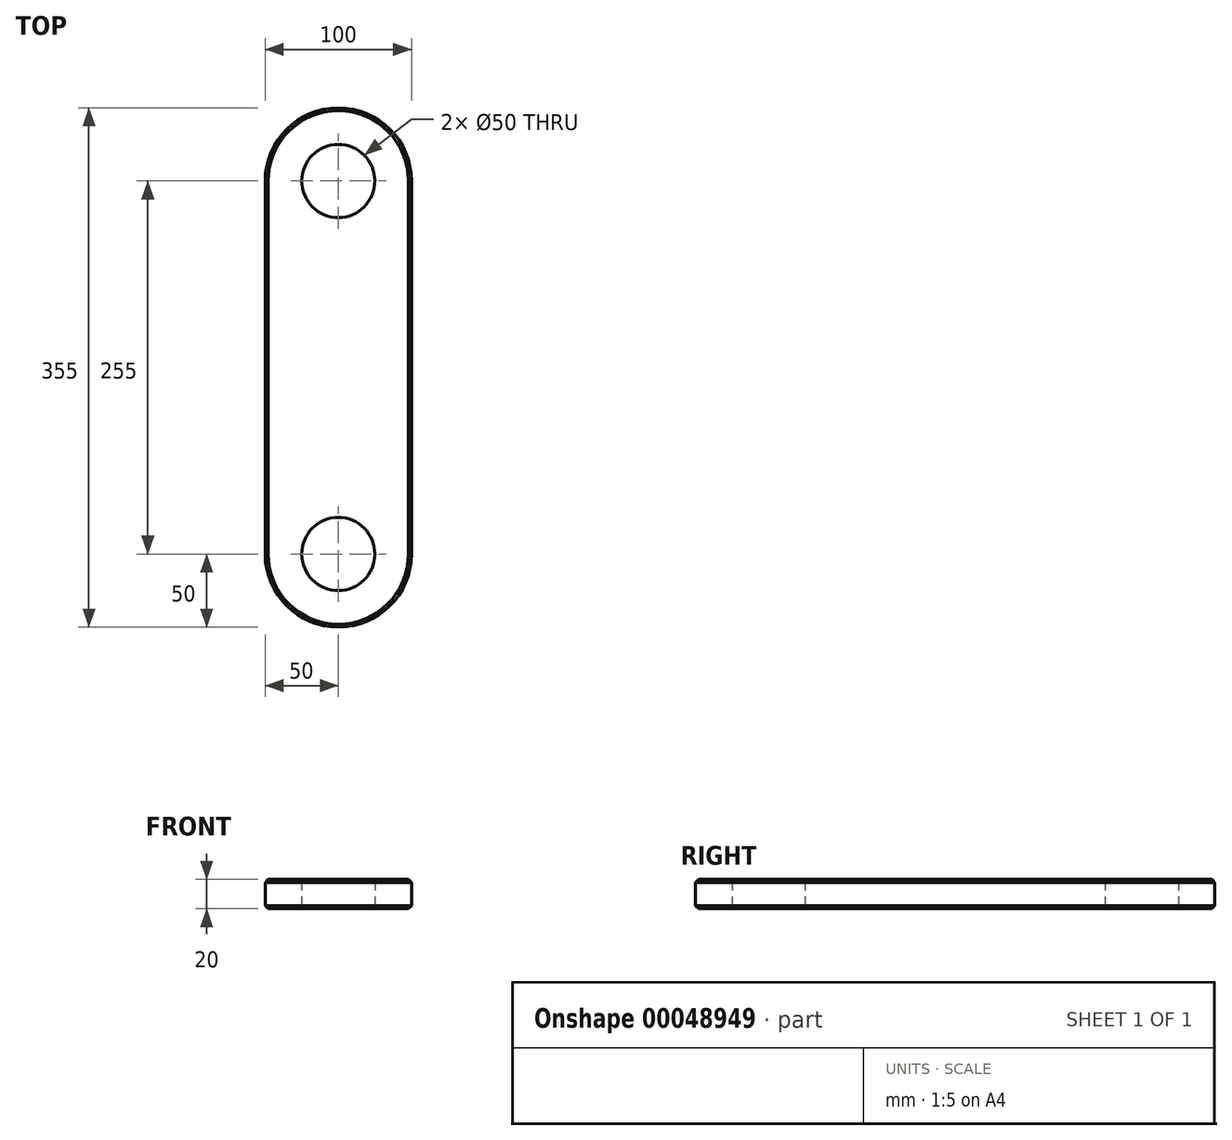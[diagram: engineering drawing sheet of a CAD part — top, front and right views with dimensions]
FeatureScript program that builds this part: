
annotation { "Feature Type Name" : "Feature", "Feature Type Description" : "" }
export const myFeature = defineFeature(function(context is Context, id is Id, definition is map)
    precondition{}
    {
        {
            var Q0;
            Q0=qCreatedBy(makeId("Top.planeOp"),FACE);
            var sketch = newSketch(context, id + "F0", { "sketchPlane" : qUnion([Q0])});
            skLineSegment(sketch, "E0.rect.bottom", {"start": v(50, 127.5) * mm, "end": v(-50, 127.5) * mm});
            skLineSegment(sketch, "E0.rect.top", {"start": v(50, -127.5) * mm, "end": v(-50, -127.5) * mm});
            skLineSegment(sketch, "E0.rect.left", {"start": v(50, 127.5) * mm, "end": v(50, -127.5) * mm});
            skLineSegment(sketch, "E0.rect.right", {"start": v(-50, 127.5) * mm, "end": v(-50, -127.5) * mm});
            skPoint(sketch, "E0.rect.middle", {"position": v(0, 0) * mm});
            skCircle(sketch, "E1", {"center": v(0, 127.5) * mm, "radius": 50 * mm});
            skCircle(sketch, "E2", {"center": v(0, -127.5) * mm, "radius": 50 * mm});
            skCircle(sketch, "E3", {"center": v(0, 127.5) * mm, "radius": 25 * mm});
            skCircle(sketch, "E4", {"center": v(0, -127.5) * mm, "radius": 25 * mm});
            skSolve(sketch);
        }
        {
            var Q0;
            {var subQ0=sQuery(id+"F0.wireOp",EDGE,"E3");var subQ1=sQuery(id+"F0.wireOp",EDGE,"E0.rect.bottom");var subQ3=makeQuery(id+"F0.imprint","INTERSECT",VERTEX,{"disambiguationData":[OD(0.0)],"derivedFrom":[subQ1,subQ0]});Q0=makeQuery(id+"F0.imprint","IMPRINT",FACE,{"disambiguationData":[TD([[makeQuery(id+"F0.imprint","IMPRINT",EDGE,{"disambiguationData":[TD([[subQ3,-1.0]])],"derivedFrom":subQ0}),-1.0]])]});}
            var Q1;
            {var subQ3=sQuery(id+"F0.wireOp",EDGE,"E0.rect.left");Q1=makeQuery(id+"F0.imprint","IMPRINT",FACE,{"disambiguationData":[TD([[makeQuery(id+"F0.imprint","IMPRINT",EDGE,{"derivedFrom":subQ3}),-1.0]])]});}
            var Q2;
            {var subQ0=sQuery(id+"F0.wireOp",EDGE,"E3");var subQ1=sQuery(id+"F0.wireOp",EDGE,"E0.rect.bottom");var subQ3=makeQuery(id+"F0.imprint","INTERSECT",VERTEX,{"disambiguationData":[OD(0.0)],"derivedFrom":[subQ1,subQ0]});Q2=makeQuery(id+"F0.imprint","IMPRINT",FACE,{"disambiguationData":[TD([[makeQuery(id+"F0.imprint","IMPRINT",EDGE,{"disambiguationData":[TD([[subQ3,1.0]])],"derivedFrom":subQ0}),-1.0]])]});}
            var Q3;
            {var subQ0=sQuery(id+"F0.wireOp",EDGE,"E4");var subQ1=sQuery(id+"F0.wireOp",EDGE,"E0.rect.top");var subQ3=makeQuery(id+"F0.imprint","INTERSECT",VERTEX,{"disambiguationData":[OD(0.0)],"derivedFrom":[subQ1,subQ0]});Q3=makeQuery(id+"F0.imprint","IMPRINT",FACE,{"disambiguationData":[TD([[makeQuery(id+"F0.imprint","IMPRINT",EDGE,{"disambiguationData":[TD([[subQ3,-1.0]])],"derivedFrom":subQ0}),-1.0]])]});}
            var Q4;
            {var subQ0=sQuery(id+"F0.wireOp",EDGE,"E4");var subQ1=sQuery(id+"F0.wireOp",EDGE,"E0.rect.top");var subQ3=makeQuery(id+"F0.imprint","INTERSECT",VERTEX,{"disambiguationData":[OD(0.0)],"derivedFrom":[subQ1,subQ0]});Q4=makeQuery(id+"F0.imprint","IMPRINT",FACE,{"disambiguationData":[TD([[makeQuery(id+"F0.imprint","IMPRINT",EDGE,{"disambiguationData":[TD([[subQ3,1.0]])],"derivedFrom":subQ0}),-1.0]])]});}
            extrude(context, id + "F1", {"entities" : qUnion([Q0, Q1, Q2, Q3, Q4]), "depth" : 20 * mm});
        }
        {
            var Q0;
            Q0=makeQuery(id+"F1.opExtrude","CAP_EDGE",EDGE,{"disambiguationData":[OSD([sQuery(id+"F0.wireOp",EDGE,"E0.rect.right")])],"isStart":false});
            var Q1;
            Q1=makeQuery(id+"F1.opExtrude","CAP_EDGE",EDGE,{"disambiguationData":[OSD([sQuery(id+"F0.wireOp",EDGE,"E1")])],"isStart":false});
            var Q2;
            Q2=makeQuery(id+"F1.opExtrude","CAP_EDGE",EDGE,{"disambiguationData":[OSD([sQuery(id+"F0.wireOp",EDGE,"E0.rect.left")])],"isStart":false});
            var Q3;
            Q3=makeQuery(id+"F1.opExtrude","CAP_EDGE",EDGE,{"disambiguationData":[OSD([sQuery(id+"F0.wireOp",EDGE,"E2")])],"isStart":false});
            var Q4;
            Q4=makeQuery(id+"F1.opExtrude","CAP_EDGE",EDGE,{"disambiguationData":[OSD([sQuery(id+"F0.wireOp",EDGE,"E2")])],"isStart":true});
            var Q5;
            Q5=makeQuery(id+"F1.opExtrude","CAP_EDGE",EDGE,{"disambiguationData":[OSD([sQuery(id+"F0.wireOp",EDGE,"E0.rect.right")])],"isStart":true});
            var Q6;
            Q6=makeQuery(id+"F1.opExtrude","CAP_EDGE",EDGE,{"disambiguationData":[OSD([sQuery(id+"F0.wireOp",EDGE,"E1")])],"isStart":true});
            var Q7;
            Q7=makeQuery(id+"F1.opExtrude","CAP_EDGE",EDGE,{"disambiguationData":[OSD([sQuery(id+"F0.wireOp",EDGE,"E0.rect.left")])],"isStart":true});
            chamfer(context, id + "F2", {"entities" : qUnion([Q0, Q1, Q2, Q3, Q4, Q5, Q6, Q7]), "chamferType" : ChamferType.OFFSET_ANGLE, "width" : 2 * mm, "oppositeDirection" : false, "angle" : 45 * degree, "tangentPropagation" : true});
        }
    });
